# Revit family: 305_R5_
name_source: partatom
category: Pipe Accessories
units: mm (PartAtom-declared; Revit-internal decimal feet)

## family parameters
Always vertical = Yes
Cut with Voids When Loaded = No
Part Type = Valve - Breaks Into
Round Connector Dimension = Use Diameter
Shared = No
Work Plane-Based = No

## types (7) — shared parameters
CAT0 = Yes
Description = Change-over ball valve, 3-way, External thread
H1 = 6 mm  [stored 0.019685 ft]
L2D_Min = 3048 mm
Manufacturer = Belimo
QmdConnectorList = 301;D;302;D;303;D
magiPartTypeId = 305
magiProductFamilyId = R5*
zero-valued in all types: MC_Default_elevation

## per-type parameters (varying)
| type | B1 | D | G2 | G3 | G4 | HH | L1 | L2 | L22 | L22__ve | L2D | LL | LL1 | M | M11 | M11__ve | MM | MM__ve | W2D |
| R515 | 19 mm  [stored 0.062336 ft] | 15 mm | 27 mm  [stored 0.0885827 ft] | 25 mm  [stored 0.082021 ft] | 20 mm  [stored 0.0656168 ft] | 38 mm | 39 mm | 15 mm  [stored 0.0492126 ft] | 7 mm  [stored 0.0229659 ft] | -7 mm | 49 mm | 25 mm  [stored 0.082021 ft] | 35 mm | 26 mm  [stored 0.0853018 ft] | 18 mm | -18 mm | 8 mm  [stored 0.0262467 ft] | -8 mm | 15 mm  [stored 0.0492126 ft] |
| R550 | 53 mm | 50 mm | 72 mm | 69 mm | 56 mm | 50 mm | 70 mm | 26 mm  [stored 0.0853018 ft] | 13 mm | -13 mm  [stored -0.0426509 ft] | 87 mm | 44 mm | 61 mm | 45 mm | 40 mm | -40 mm | 5 mm  [stored 0.0164042 ft] | -5 mm  [stored -0.0164042 ft] | 50 mm |
| R540 | 45 mm | 40 mm | 62 mm | 59 mm | 48 mm | 45 mm | 61 mm | 23 mm | 11 mm | -11 mm | 76 mm | 38 mm | 53 mm | 37 mm | 35 mm | -35 mm | 2 mm  [stored 0.00656168 ft] | -2 mm  [stored -0.00656168 ft] | 40 mm |
| R532 | 38 mm | 32 mm | 52 mm | 49 mm | 40 mm | 45 mm | 57 mm | 21 mm | 11 mm | -11 mm | 71 mm | 36 mm | 50 mm | 37 mm | 31 mm | -31 mm | 7 mm  [stored 0.0229659 ft] | -7 mm | 32 mm |
| R530 | 38 mm | 32 mm | 52 mm | 49 mm | 40 mm | 40 mm | 55 mm | 21 mm | 10 mm  [stored 0.0328084 ft] | -10 mm  [stored -0.0328084 ft] | 69 mm | 35 mm | 48 mm | 37 mm | 31 mm | -31 mm | 7 mm  [stored 0.0229659 ft] | -7 mm | 32 mm |
| R525 | 30 mm  [stored 0.0984252 ft] | 25 mm | 42 mm | 39 mm | 32 mm | 40 mm | 45 mm | 17 mm | 8 mm  [stored 0.0262467 ft] | -8 mm | 56 mm | 28 mm  [stored 0.0918635 ft] | 39 mm | 30 mm  [stored 0.0984252 ft] | 26 mm  [stored 0.0853018 ft] | -26 mm  [stored -0.0853018 ft] | 4 mm | -4 mm | 25 mm  [stored 0.082021 ft] |
| R520 | 24 mm  [stored 0.0787402 ft] | 20 mm | 34 mm | 31 mm | 26 mm  [stored 0.0853018 ft] | 40 mm | 45 mm | 17 mm | 8 mm  [stored 0.0262467 ft] | -8 mm | 56 mm | 28 mm  [stored 0.0918635 ft] | 40 mm | 28 mm  [stored 0.0918635 ft] | 22 mm | -22 mm | 6 mm  [stored 0.019685 ft] | -6 mm | 20 mm  [stored 0.0656168 ft] |

note: column(s) folded — value = type name in every type: magiProductCode, magiProductId

note: [stored X ft] marks values corroborated as IEEE doubles in the binary element streams (Revit-internal decimal feet)

## geometry (parser evidence)
native form markers: Sweep x2
no freeform markers — native parametric forms only
